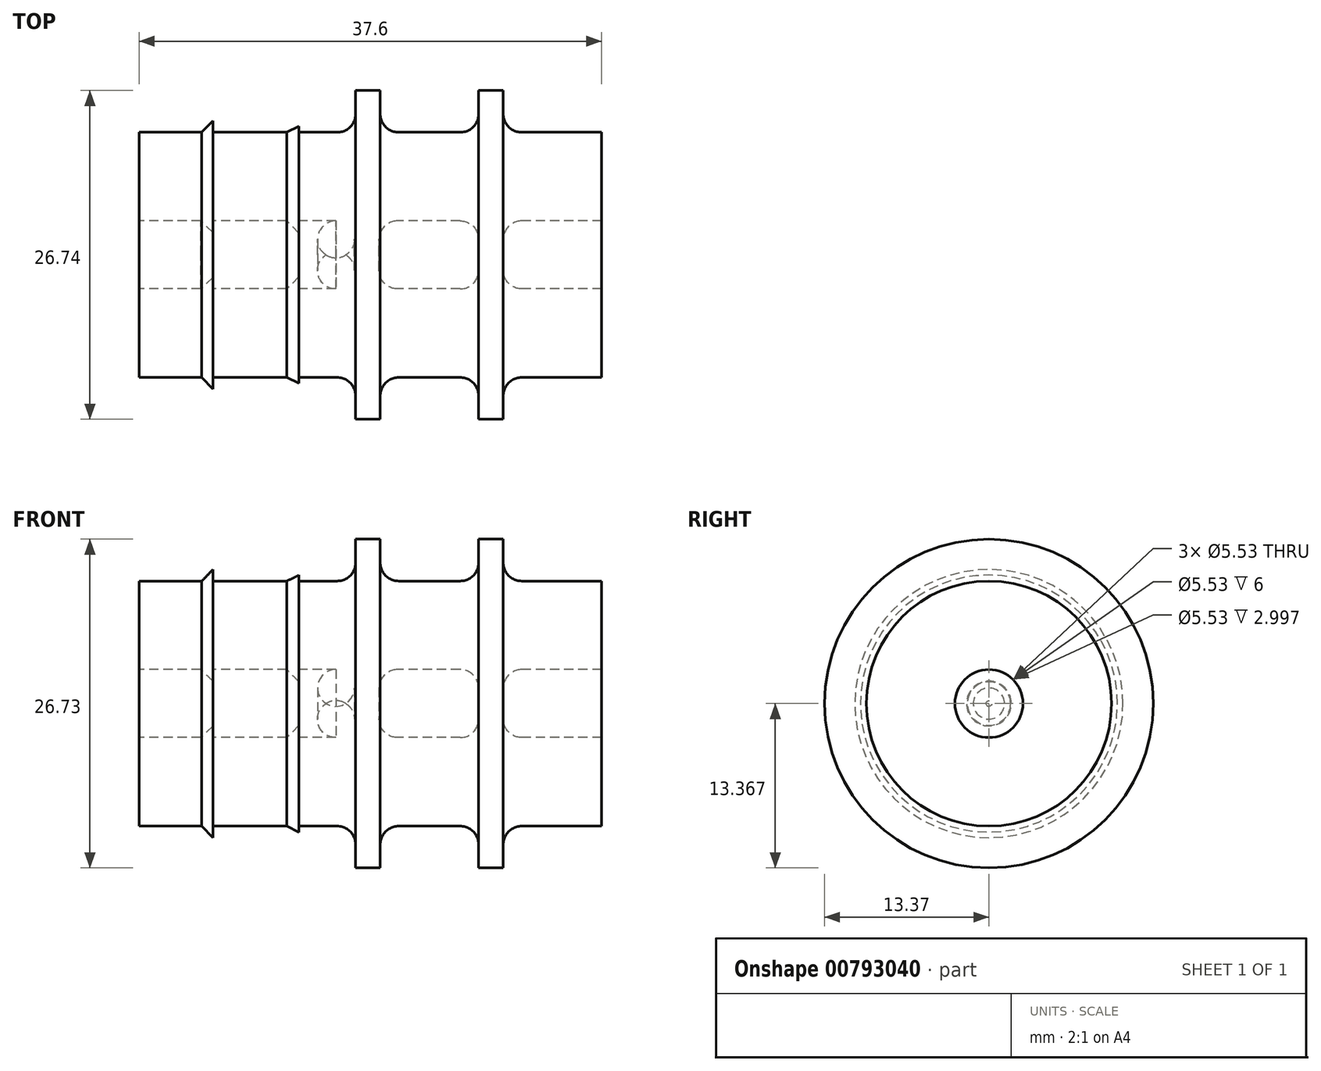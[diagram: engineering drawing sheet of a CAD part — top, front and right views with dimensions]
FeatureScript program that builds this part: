
annotation { "Feature Type Name" : "Feature", "Feature Type Description" : "" }
export const myFeature = defineFeature(function(context is Context, id is Id, definition is map)
    precondition{}
    {
        {
            var Q0;
            Q0=qCreatedBy(makeId("Front.planeOp"),FACE);
            var sketch = newSketch(context, id + "F0", { "sketchPlane" : qUnion([Q0])});
            skLineSegment(sketch, "E0", {"start": v(0.09, -2.13) * mm, "end": v(0, -2.13) * mm});
            skLineSegment(sketch, "E1", {"start": v(3.37, -3.63) * mm, "end": v(3.37, -5.53) * mm});
            skLineSegment(sketch, "E2", {"start": v(3.37, -5.53) * mm, "end": v(1.37, -5.53) * mm});
            skLineSegment(sketch, "E3", {"start": v(1.37, -5.53) * mm, "end": v(1.37, -3.63) * mm});
            skLineSegment(sketch, "E4", {"start": v(-0.13, -2.13) * mm, "end": v(-5.13, -2.13) * mm});
            skLineSegment(sketch, "E5", {"start": v(-6.63, -3.63) * mm, "end": v(-6.63, -5.53) * mm});
            skLineSegment(sketch, "E6", {"start": v(-6.63, -5.53) * mm, "end": v(-8.63, -5.53) * mm});
            skLineSegment(sketch, "E7", {"start": v(-8.63, -5.53) * mm, "end": v(-8.63, -3.63) * mm});
            skLineSegment(sketch, "E8", {"start": v(-10.13, -2.13) * mm, "end": v(-26.23, -2.13) * mm});
            skLineSegment(sketch, "E9", {"start": v(-26.23, -2.13) * mm, "end": v(-26.23, 5.07) * mm});
            skLineSegment(sketch, "E10", {"start": v(-26.23, 5.07) * mm, "end": v(-10.23, 5.07) * mm});
            skLineSegment(sketch, "E11", {"start": v(-8.73, 6.57) * mm, "end": v(-8.73, 7.84) * mm});
            skLineSegment(sketch, "E12", {"start": v(-8.73, 7.84) * mm, "end": v(-6.73, 7.84) * mm});
            skLineSegment(sketch, "E13", {"start": v(-6.73, 7.84) * mm, "end": v(-6.73, 6.57) * mm});
            skLineSegment(sketch, "E14", {"start": v(-5.23, 5.07) * mm, "end": v(-0.13, 5.07) * mm});
            skLineSegment(sketch, "E15", {"start": v(1.37, 6.57) * mm, "end": v(1.37, 7.84) * mm});
            skLineSegment(sketch, "E16", {"start": v(1.37, 7.84) * mm, "end": v(3.37, 7.84) * mm});
            skLineSegment(sketch, "E17", {"start": v(3.37, 7.84) * mm, "end": v(3.37, 6.57) * mm});
            skLineSegment(sketch, "E18", {"start": v(0, 5.07) * mm, "end": v(0.09, 5.07) * mm});
            skLineSegment(sketch, "E19", {"start": v(4.87, -2.13) * mm, "end": v(11.37, -2.13) * mm});
            skLineSegment(sketch, "E20", {"start": v(11.37, -2.13) * mm, "end": v(11.37, 5.07) * mm});
            skLineSegment(sketch, "E21", {"start": v(11.37, 5.07) * mm, "end": v(4.87, 5.07) * mm});
            skLineSegment(sketch, "E22", {"start": v(-13.23, -2.13) * mm, "end": v(-13.23, -2.61) * mm});
            skLineSegment(sketch, "E23", {"start": v(-13.23, -2.61) * mm, "end": v(-14.23, -2.13) * mm});
            skLineSegment(sketch, "E24", {"start": v(-13.23, 5.07) * mm, "end": v(-13.23, 6.07) * mm});
            skLineSegment(sketch, "E25", {"start": v(-13.23, 6.07) * mm, "end": v(-14.23, 5.07) * mm});
            skLineSegment(sketch, "E26", {"start": v(-20.23, -2.13) * mm, "end": v(-20.23, -3.06) * mm});
            skLineSegment(sketch, "E27", {"start": v(-20.23, -3.06) * mm, "end": v(-21.14, -2.13) * mm});
            skLineSegment(sketch, "E28", {"start": v(-20.23, 5.07) * mm, "end": v(-20.23, 6.02) * mm});
            skLineSegment(sketch, "E29", {"start": v(-20.23, 6.02) * mm, "end": v(-21.21, 5.07) * mm});
            skArc(sketch, "E30.filletArc", {"start": v(4.87, -2.13) * mm, "mid": v(3.81, -2.57) * mm, "end": v(3.37, -3.63) * mm});
            skPoint(sketch, "E31.visualSharp", {"position": v(1.37, -2.13) * mm});
            skArc(sketch, "E31.filletArc", {"start": v(1.37, -3.63) * mm, "mid": v(0.93, -2.57) * mm, "end": v(-0.13, -2.13) * mm});
            skPoint(sketch, "E32.visualSharp", {"position": v(-6.63, -2.13) * mm});
            skArc(sketch, "E32.filletArc", {"start": v(-5.13, -2.13) * mm, "mid": v(-6.19, -2.57) * mm, "end": v(-6.63, -3.63) * mm});
            skPoint(sketch, "E33.visualSharp", {"position": v(-8.63, -2.13) * mm});
            skArc(sketch, "E33.filletArc", {"start": v(-8.63, -3.63) * mm, "mid": v(-9.07, -2.57) * mm, "end": v(-10.13, -2.13) * mm});
            skPoint(sketch, "E34.visualSharp", {"position": v(-8.73, 5.07) * mm});
            skArc(sketch, "E34.filletArc", {"start": v(-10.23, 5.07) * mm, "mid": v(-9.17, 5.51) * mm, "end": v(-8.73, 6.57) * mm});
            skPoint(sketch, "E35.visualSharp", {"position": v(-6.73, 5.07) * mm});
            skArc(sketch, "E35.filletArc", {"start": v(-6.73, 6.57) * mm, "mid": v(-6.3, 5.51) * mm, "end": v(-5.23, 5.07) * mm});
            skPoint(sketch, "E36.visualSharp", {"position": v(1.37, 5.07) * mm});
            skArc(sketch, "E36.filletArc", {"start": v(-0.13, 5.07) * mm, "mid": v(0.93, 5.51) * mm, "end": v(1.37, 6.57) * mm});
            skPoint(sketch, "E37.newPointB", {"position": v(3.37, 5.07) * mm});
            skArc(sketch, "E37.filletArc", {"start": v(3.37, 6.57) * mm, "mid": v(3.81, 5.51) * mm, "end": v(4.87, 5.07) * mm});
            skSolve(sketch);
        }
        {
            var Q0;
            Q0 = qSketchRegion(id + "F0", true);
            var Q1;
            Q1=sQuery(id+"F0.wireOp",EDGE,"E16");
            revolve(context, id + "F1", {"surfaceOperationType" : NewSurfaceOperationType.NEW, "entities" : qUnion([Q0]), "axis" : qUnion([Q1]), "revolveType" : RevolveType.FULL});
        }
    });
